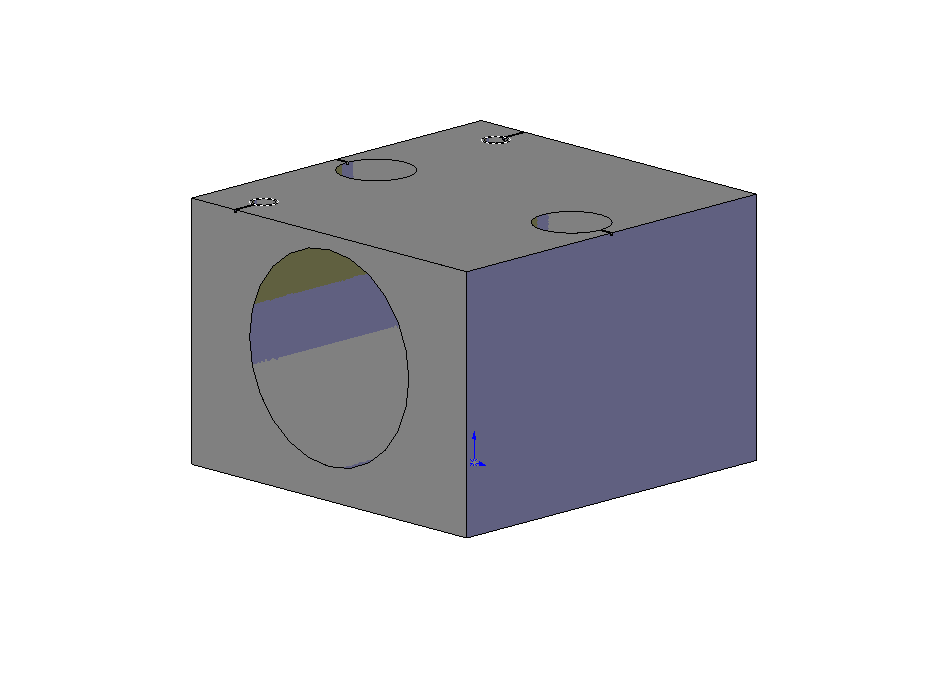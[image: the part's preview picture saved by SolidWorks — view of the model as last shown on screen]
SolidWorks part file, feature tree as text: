
SOLIDWORKS PART (.sldprt)
format: sldprt  version: not decoded by parser v0  size: 467,968 bytes
history: native  units: mm
features: sketch x7, cut_extrude x2, hole x2, thread x2, material x1, extrude x1 + 1 further entry (+11 scaffold rows collapsed)
feature tree (27):
  scaffold x11  (default folders/planes/origin — collapsed)
  material  "6061 Alloy"
  "Origin"  ID=-1
  sketch  "Sketch1"  dims[D1=38.0mm D2=27.0mm]
  extrude  "Extrude1"  Depth=40mm
  sketch  "Sketch2"  dims[D1=22.0mm D2=14.5mm]
  cut_extrude  "Light-Weighting Hole"  [1 undecoded]
  hole  "#4-40 Tapped Hole1"  Diameter=2.2606mm Depth=8.8646mm
  sketch  "Sketch5"  dims[D1=32.0mm D2=6.0mm]
  sketch  "Sketch4"  dims[hole-wizard template sketch: 47 standard entries collapsed; hole parameters kept: c15.Tap Drill Depth=8.8646mm c15.D3=~14.816244mm c15.Drill Angle=118.0deg]
  thread  "Cosmetic Thread1"  Diameter=5.6896mm  [1 undecoded]
  thread  "Cosmetic Thread2"  Diameter=5.6896mm  [1 undecoded]
  hole  "CBORE for #8 Socket Head Cap Screw1"  Diameter=4.3053mm Depth=27mm
  sketch  "Sketch8"  dims[D1=27.0mm D2=~30.232948mm]
  sketch  "Sketch7"  dims[hole-wizard template sketch: 41 standard entries collapsed; hole parameters kept: c12.Thru Hole Dia.=4.3053mm c12.Thru Hole Depth=27.0mm c12.C'Bore Dia.=7.9375mm c12.C'Bore Depth=4.1656mm]
  sketch  "Sketch9"  dims[D1=0.25mm D2=0.25mm D3=0.25mm D4=0.25mm D5=4.0mm]
  cut_extrude  "Cut-Extrude1"  Depth=0.25mm
decode coverage: 13 of 14 modeling features carry decoded parameters; 1 rows unclassified (native names shown)
note: ~ marks probable driven/reference dimensions
note: 3 parameter values undecoded
note: suppression state not decoded; provenance and decode notes live in map.json
